# Revit family: P500226-141
name_source: partatom
category: Lighting Fixtures
revit_build: Autodesk Revit 2014 (Build: 20130308_1515(x64)
units: mm (PartAtom-declared; Revit-internal decimal feet)

## types (1)
- P500226-141
    Apparent Load = 100 VA
    Assembly Code = D5020200
    Color Filter = 16777215
    Connector Description = Lighting Connector
    Default Elevation = 48"
    Description = Create a countrified home that will make any guest want to stay for a cozy cup of tea and a warm slice of apple pie with this pendant. The clear seeded glass shade creates a rustic atmosphere that is all about comfort and charm. The galvanized finish is inspired by modern farmhouse-style decor.
    Diameter = 9 1/4"
    Dimming Lamp Color Temperature Shift = <None>
    Fixture distribution = Direct
    Glass = Hubbell - Glass
    Gold = Hubbell - Gold
    Height = 11 1/8"
    Housing Material = Paint - Hubbell -Steel
    Lamp = A-19 or LED
    Load Classification = Lighting
    Manufacturer = Progress Lighting
    Model = P500226-141
    Photometric Web File = generic
    Power Factor = 1
    Product Documentation Link = https://hubbellcdn.com
    Product Link = https://www.hubbell.com
    Specifications = The clear seeded glass shade creates a rustic atmosphere that is all about comfort and charm.
The galvanized finish is inspired by modern farmhouse-style decor.
Create a countrified home that will make any guest want to stay for a cozy cup of tea and a warm slice of apple pie with this pendant.
Ideal for any foyer, entryway, patio, or porch.
Perfect for rustic and farmhouse settings.
Measures 9-1/4-inch width by 11-1/8-inch height.
Uses one medium base bulb that is sold separately (100w max - LED or incandescent).
Able to be fully dimmable with dimmable bulbs.
Includes installation instructions and mounting hardware.
Progress Lighting products are designed for exceptional quality, reliability, and functionality.
    Tilt Angle = 60.00°
    URL = https://www.hubbell.com
    Voltage = 120 V
    Warranty = 5 years Warranty
    Wattage Comments = 100W
    Watts = 100 W
    White = Paint - Hubbell - Matte White

## geometry (parser evidence)
native form markers: Sweep x6
no freeform markers — native parametric forms only
